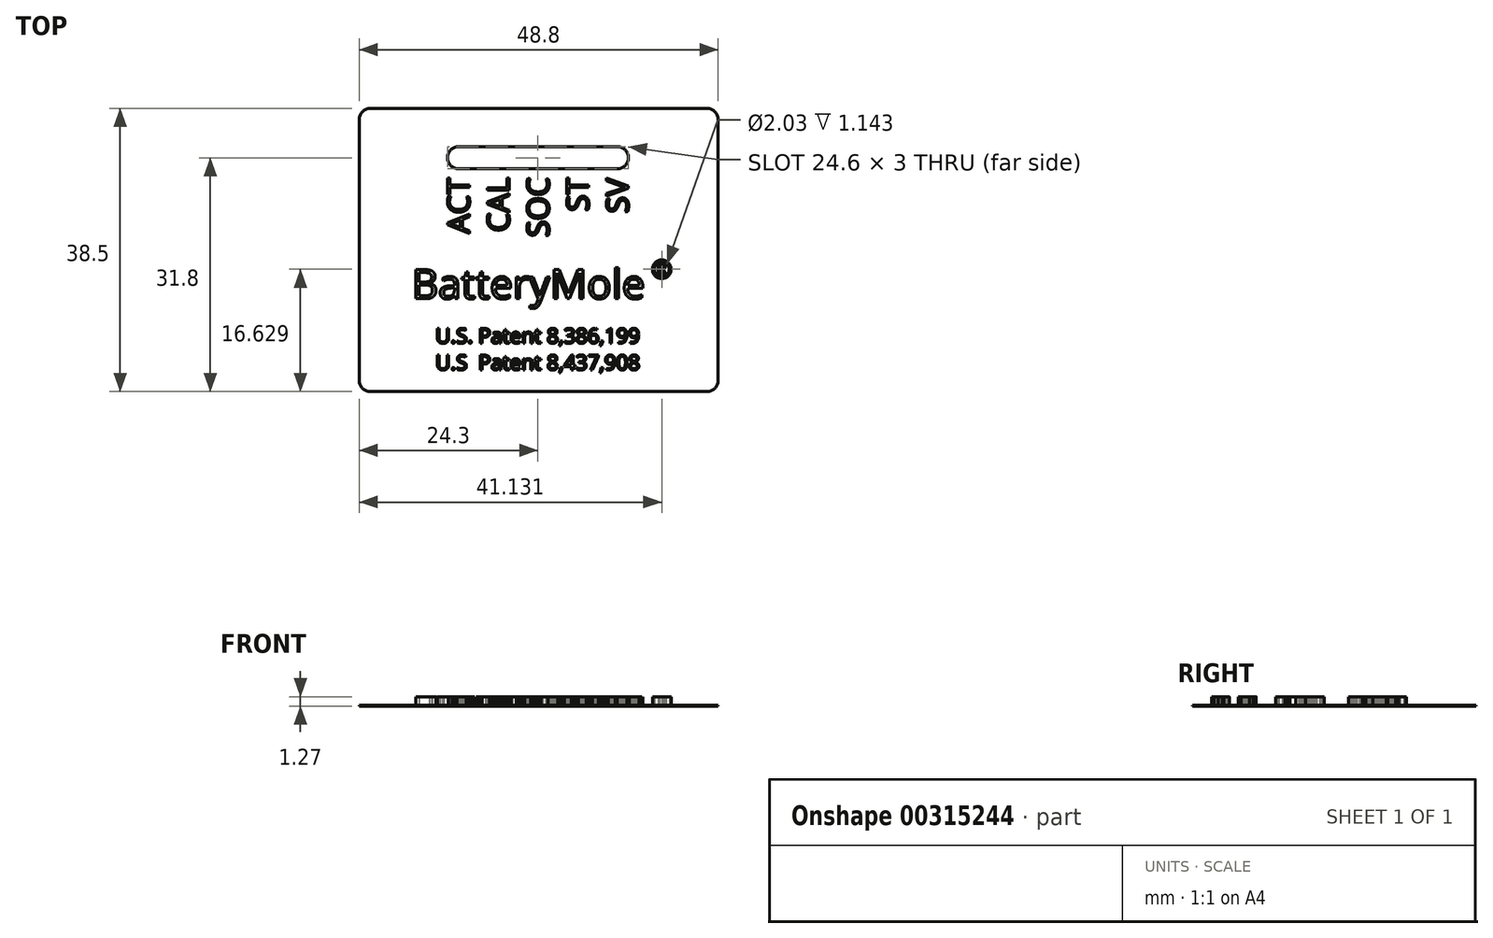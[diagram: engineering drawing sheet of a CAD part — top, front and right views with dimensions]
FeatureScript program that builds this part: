
annotation { "Feature Type Name" : "Feature", "Feature Type Description" : "" }
export const myFeature = defineFeature(function(context is Context, id is Id, definition is map)
    precondition{}
    {
        {
            var Q0;
            Q0=qCreatedBy(makeId("Top.planeOp"),FACE);
            var sketch = newSketch(context, id + "F0", { "sketchPlane" : qUnion([Q0])});
            skLineSegment(sketch, "E0.bottom", {"start": v(1.5, 38.5) * mm, "end": v(47.3, 38.5) * mm});
            skLineSegment(sketch, "E0.top", {"start": v(1.5, 0) * mm, "end": v(47.3, 0) * mm});
            skLineSegment(sketch, "E0.left", {"start": v(0, 37) * mm, "end": v(0, 1.5) * mm});
            skLineSegment(sketch, "E0.right", {"start": v(48.8, 37) * mm, "end": v(48.8, 1.5) * mm});
            skPoint(sketch, "E1.visualSharp", {"position": v(0, 38.5) * mm});
            skArc(sketch, "E1.filletArc", {"start": v(1.5, 38.5) * mm, "mid": v(0.44, 38.06) * mm, "end": v(0, 37) * mm});
            skPoint(sketch, "E2.visualSharp", {"position": v(48.8, 38.5) * mm});
            skArc(sketch, "E2.filletArc", {"start": v(48.8, 37) * mm, "mid": v(48.36, 38.06) * mm, "end": v(47.3, 38.5) * mm});
            skPoint(sketch, "E3.visualSharp", {"position": v(48.8, 0) * mm});
            skArc(sketch, "E3.filletArc", {"start": v(47.3, 0) * mm, "mid": v(48.36, 0.44) * mm, "end": v(48.8, 1.5) * mm});
            skPoint(sketch, "E4.visualSharp", {"position": v(0, 0) * mm});
            skArc(sketch, "E4.filletArc", {"start": v(0, 1.5) * mm, "mid": v(0.44, 0.44) * mm, "end": v(1.5, 0) * mm});
            skLineSegment(sketch, "E5", {"start": v(-1.94, 31.8) * mm, "end": v(50.94, 31.8) * mm, "construction": true});
            skPoint(sketch, "E6", {"position": v(0, 19.25) * mm});
            skLineSegment(sketch, "E7", {"start": v(24.3, 31.8) * mm, "end": v(24.3, 57.95) * mm, "construction": true});
            skLineSegment(sketch, "E8", {"start": v(41.58, 29.3) * mm, "end": v(3.43, 29.3) * mm, "construction": true});
            skArc(sketch, "E9", {"start": v(13.5, 33.3) * mm, "mid": v(12, 31.8) * mm, "end": v(13.5, 30.3) * mm});
            skArc(sketch, "E10", {"start": v(35.1, 33.3) * mm, "mid": v(36.6, 31.8) * mm, "end": v(35.1, 30.3) * mm});
            skLineSegment(sketch, "E11", {"start": v(13.5, 33.3) * mm, "end": v(35.1, 33.3) * mm});
            skLineSegment(sketch, "E12", {"start": v(35.1, 30.3) * mm, "end": v(13.5, 30.3) * mm});
            skSolve(sketch);
        }
        {
            var Q0;
            Q0=qCreatedBy(makeId("Top.planeOp"),FACE);
            var sketch = newSketch(context, id + "F1", { "sketchPlane" : qUnion([Q0])});
            skLineSegment(sketch, "E13.bottom", {"start": v(1.5, 38.5) * mm, "end": v(47.3, 38.5) * mm});
            skLineSegment(sketch, "E13.top", {"start": v(1.5, 0) * mm, "end": v(47.3, 0) * mm});
            skLineSegment(sketch, "E13.left", {"start": v(0, 37) * mm, "end": v(0, 1.5) * mm});
            skLineSegment(sketch, "E13.right", {"start": v(48.8, 37) * mm, "end": v(48.8, 1.5) * mm});
            skPoint(sketch, "E14.visualSharp", {"position": v(0, 38.5) * mm});
            skArc(sketch, "E14.filletArc", {"start": v(1.5, 38.5) * mm, "mid": v(0.44, 38.06) * mm, "end": v(0, 37) * mm});
            skPoint(sketch, "E15.visualSharp", {"position": v(48.8, 38.5) * mm});
            skArc(sketch, "E15.filletArc", {"start": v(48.8, 37) * mm, "mid": v(48.36, 38.06) * mm, "end": v(47.3, 38.5) * mm});
            skPoint(sketch, "E16.visualSharp", {"position": v(48.8, 0) * mm});
            skArc(sketch, "E16.filletArc", {"start": v(47.3, 0) * mm, "mid": v(48.36, 0.44) * mm, "end": v(48.8, 1.5) * mm});
            skPoint(sketch, "E17.visualSharp", {"position": v(0, 0) * mm});
            skArc(sketch, "E17.filletArc", {"start": v(0, 1.5) * mm, "mid": v(0.44, 0.44) * mm, "end": v(1.5, 0) * mm});
            skText(sketch, "E18", { "text": "BatteryMole", "fontName": "OpenSans-Regular.ttf"});
            skCircle(sketch, "E19", {"center": v(41.13, 16.63) * mm, "radius": 1.02 * mm});
            skCircle(sketch, "E20", {"center": v(41.13, 16.63) * mm, "radius": 1.27 * mm});
            skText(sketch, "E21", { "text": "U.S. Patent 8,386,199", "fontName": "OpenSans-Regular.ttf"});
            skText(sketch, "E22", { "text": "U.S. Patent 8,437,908", "fontName": "OpenSans-Regular.ttf"});
            skPoint(sketch, "E23", {"position": v(0, 19.25) * mm});
            skLineSegment(sketch, "E24", {"start": v(24.3, 16.46) * mm, "end": v(24.3, 31.8) * mm, "construction": true});
            skText(sketch, "E25", { "text": "ACT", "fontName": "OpenSans-Regular.ttf"});
            skText(sketch, "E26", { "text": "CAL", "fontName": "OpenSans-Regular.ttf"});
            skText(sketch, "E27", { "text": "SV", "fontName": "OpenSans-Regular.ttf"});
            skText(sketch, "E28", { "text": "ST", "fontName": "OpenSans-Regular.ttf"});
            skLineSegment(sketch, "E29", {"start": v(41.58, 29.3) * mm, "end": v(3.43, 29.3) * mm, "construction": true});
            skText(sketch, "E30", { "text": "R", "fontName": "OpenSans-Regular.ttf"});
            skText(sketch, "E31", { "text": "SOC", "fontName": "OpenSans-Regular.ttf"});
            skPoint(sketch, "E32", {"position": v(24.3, 21) * mm});
            const initialGuessF1  = {"E18": [0.00715, 0.01263, 1, 0, 0.004], "E21": [0.01037, 0.00658, 1, 0, 0.00203], "E22": [0.01037, 0.00295, 1, 0, 0.00203], "E25": [0.015, 0.0215, 0, 1, 0.003], "E26": [0.0204, 0.0217, 0, 1, 0.003], "E27": [0.0366, 0.02426, 0, 1, 0.003], "E28": [0.0312, 0.02448, 0, 1, 0.003], "E30": [0.04045, 0.0159, 1, 0, 0.0015], "E31": [0.0258, 0.021, 0, 1, 0.003]};
            skSetInitialGuess(sketch, initialGuessF1);
            skSolve(sketch);
        }
        {
            var Q0;
            Q0=makeQuery(id+"F0.imprint","IMPRINT",FACE,{"disambiguationData":[TD([[makeQuery(id+"F0.imprint","IMPRINT",EDGE,{"derivedFrom":sQuery(id+"F0.wireOp",EDGE,"E0.bottom")}),-1.0]])]});
            extrude(context, id + "F2", {"entities" : qUnion([Q0]), "depth" : 0.13 * mm});
        }
        {
            var Q0;
            Q0=makeQuery(id+"F1.imprint","IMPRINT",FACE,{"disambiguationData":[TD([[makeQuery(id+"F1.imprint","IMPRINT",EDGE,{"derivedFrom":sQuery(id+"F1.wireOp",EDGE,"E21.sketch_text.stroke-0")}),-1.0]])]});
            var Q1;
            Q1=makeQuery(id+"F1.imprint","IMPRINT",FACE,{"disambiguationData":[TD([[makeQuery(id+"F1.imprint","IMPRINT",EDGE,{"derivedFrom":sQuery(id+"F1.wireOp",EDGE,"E21.sketch_text.stroke-14")}),-1.0]])]});
            var Q2;
            Q2=makeQuery(id+"F1.imprint","IMPRINT",FACE,{"disambiguationData":[TD([[makeQuery(id+"F1.imprint","IMPRINT",EDGE,{"derivedFrom":sQuery(id+"F1.wireOp",EDGE,"E21.sketch_text.stroke-22")}),-1.0]])]});
            var Q3;
            Q3=makeQuery(id+"F1.imprint","IMPRINT",FACE,{"disambiguationData":[TD([[makeQuery(id+"F1.imprint","IMPRINT",EDGE,{"derivedFrom":sQuery(id+"F1.wireOp",EDGE,"E21.sketch_text.stroke-47")}),-1.0]])]});
            var Q4;
            Q4=makeQuery(id+"F1.imprint","IMPRINT",FACE,{"disambiguationData":[TD([[makeQuery(id+"F1.imprint","IMPRINT",EDGE,{"derivedFrom":sQuery(id+"F1.wireOp",EDGE,"E21.sketch_text.stroke-55")}),-1.0]])]});
            var Q5;
            Q5=makeQuery(id+"F1.imprint","IMPRINT",FACE,{"disambiguationData":[TD([[makeQuery(id+"F1.imprint","IMPRINT",EDGE,{"derivedFrom":sQuery(id+"F1.wireOp",EDGE,"E21.sketch_text.stroke-70")}),-1.0]])]});
            var Q6;
            Q6=makeQuery(id+"F1.imprint","IMPRINT",FACE,{"disambiguationData":[TD([[makeQuery(id+"F1.imprint","IMPRINT",EDGE,{"derivedFrom":sQuery(id+"F1.wireOp",EDGE,"E21.sketch_text.stroke-97")}),-1.0]])]});
            var Q7;
            Q7=makeQuery(id+"F1.imprint","IMPRINT",FACE,{"disambiguationData":[TD([[makeQuery(id+"F1.imprint","IMPRINT",EDGE,{"derivedFrom":sQuery(id+"F1.wireOp",EDGE,"E21.sketch_text.stroke-116")}),-1.0]])]});
            var Q8;
            Q8=makeQuery(id+"F1.imprint","IMPRINT",FACE,{"disambiguationData":[TD([[makeQuery(id+"F1.imprint","IMPRINT",EDGE,{"derivedFrom":sQuery(id+"F1.wireOp",EDGE,"E21.sketch_text.stroke-135")}),-1.0]])]});
            var Q9;
            Q9=makeQuery(id+"F1.imprint","IMPRINT",FACE,{"disambiguationData":[TD([[makeQuery(id+"F1.imprint","IMPRINT",EDGE,{"derivedFrom":sQuery(id+"F1.wireOp",EDGE,"E22.sketch_text.stroke-152")}),-1.0]])]});
            var Q10;
            Q10=makeQuery(id+"F1.imprint","IMPRINT",FACE,{"disambiguationData":[TD([[makeQuery(id+"F1.imprint","IMPRINT",EDGE,{"derivedFrom":sQuery(id+"F1.wireOp",EDGE,"E22.sketch_text.stroke-135")}),-1.0]])]});
            var Q11;
            Q11=makeQuery(id+"F1.imprint","IMPRINT",FACE,{"disambiguationData":[TD([[makeQuery(id+"F1.imprint","IMPRINT",EDGE,{"derivedFrom":sQuery(id+"F1.wireOp",EDGE,"E22.sketch_text.stroke-116")}),-1.0]])]});
            var Q12;
            Q12=makeQuery(id+"F1.imprint","IMPRINT",FACE,{"disambiguationData":[TD([[makeQuery(id+"F1.imprint","IMPRINT",EDGE,{"derivedFrom":sQuery(id+"F1.wireOp",EDGE,"E22.sketch_text.stroke-97")}),-1.0]])]});
            var Q13;
            Q13=makeQuery(id+"F1.imprint","IMPRINT",FACE,{"disambiguationData":[TD([[makeQuery(id+"F1.imprint","IMPRINT",EDGE,{"derivedFrom":sQuery(id+"F1.wireOp",EDGE,"E22.sketch_text.stroke-70")}),-1.0]])]});
            var Q14;
            Q14=makeQuery(id+"F1.imprint","IMPRINT",FACE,{"disambiguationData":[TD([[makeQuery(id+"F1.imprint","IMPRINT",EDGE,{"derivedFrom":sQuery(id+"F1.wireOp",EDGE,"E22.sketch_text.stroke-55")}),-1.0]])]});
            var Q15;
            Q15=makeQuery(id+"F1.imprint","IMPRINT",FACE,{"disambiguationData":[TD([[makeQuery(id+"F1.imprint","IMPRINT",EDGE,{"derivedFrom":sQuery(id+"F1.wireOp",EDGE,"E22.sketch_text.stroke-0")}),-1.0]])]});
            var Q16;
            Q16=makeQuery(id+"F1.imprint","IMPRINT",FACE,{"disambiguationData":[TD([[makeQuery(id+"F1.imprint","IMPRINT",EDGE,{"derivedFrom":sQuery(id+"F1.wireOp",EDGE,"E22.sketch_text.stroke-14")}),-1.0]])]});
            var Q17;
            Q17=makeQuery(id+"F1.imprint","IMPRINT",FACE,{"disambiguationData":[TD([[makeQuery(id+"F1.imprint","IMPRINT",EDGE,{"derivedFrom":sQuery(id+"F1.wireOp",EDGE,"E22.sketch_text.stroke-22")}),-1.0]])]});
            var Q18;
            Q18=makeQuery(id+"F1.imprint","IMPRINT",FACE,{"disambiguationData":[TD([[makeQuery(id+"F1.imprint","IMPRINT",EDGE,{"derivedFrom":sQuery(id+"F1.wireOp",EDGE,"E22.sketch_text.stroke-310")}),-1.0]])]});
            var Q19;
            Q19=makeQuery(id+"F1.imprint","IMPRINT",FACE,{"disambiguationData":[TD([[makeQuery(id+"F1.imprint","IMPRINT",EDGE,{"derivedFrom":sQuery(id+"F1.wireOp",EDGE,"E22.sketch_text.stroke-294")}),-1.0]])]});
            var Q20;
            Q20=makeQuery(id+"F1.imprint","IMPRINT",FACE,{"disambiguationData":[TD([[makeQuery(id+"F1.imprint","IMPRINT",EDGE,{"derivedFrom":sQuery(id+"F1.wireOp",EDGE,"E22.sketch_text.stroke-268")}),-1.0]])]});
            var Q21;
            Q21=makeQuery(id+"F1.imprint","IMPRINT",FACE,{"disambiguationData":[TD([[makeQuery(id+"F1.imprint","IMPRINT",EDGE,{"derivedFrom":sQuery(id+"F1.wireOp",EDGE,"E22.sketch_text.stroke-261")}),-1.0]])]});
            var Q22;
            Q22=makeQuery(id+"F1.imprint","IMPRINT",FACE,{"disambiguationData":[TD([[makeQuery(id+"F1.imprint","IMPRINT",EDGE,{"derivedFrom":sQuery(id+"F1.wireOp",EDGE,"E22.sketch_text.stroke-254")}),-1.0]])]});
            var Q23;
            Q23=makeQuery(id+"F1.imprint","IMPRINT",FACE,{"disambiguationData":[TD([[makeQuery(id+"F1.imprint","IMPRINT",EDGE,{"derivedFrom":sQuery(id+"F1.wireOp",EDGE,"E22.sketch_text.stroke-226")}),-1.0]])]});
            var Q24;
            Q24=makeQuery(id+"F1.imprint","IMPRINT",FACE,{"disambiguationData":[TD([[makeQuery(id+"F1.imprint","IMPRINT",EDGE,{"derivedFrom":sQuery(id+"F1.wireOp",EDGE,"E22.sketch_text.stroke-209")}),-1.0]])]});
            var Q25;
            Q25=makeQuery(id+"F1.imprint","IMPRINT",FACE,{"disambiguationData":[TD([[makeQuery(id+"F1.imprint","IMPRINT",EDGE,{"derivedFrom":sQuery(id+"F1.wireOp",EDGE,"E21.sketch_text.stroke-209")}),-1.0]])]});
            var Q26;
            Q26=makeQuery(id+"F1.imprint","IMPRINT",FACE,{"disambiguationData":[TD([[makeQuery(id+"F1.imprint","IMPRINT",EDGE,{"derivedFrom":sQuery(id+"F1.wireOp",EDGE,"E21.sketch_text.stroke-237")}),-1.0]])]});
            var Q27;
            Q27=makeQuery(id+"F1.imprint","IMPRINT",FACE,{"disambiguationData":[TD([[makeQuery(id+"F1.imprint","IMPRINT",EDGE,{"derivedFrom":sQuery(id+"F1.wireOp",EDGE,"E21.sketch_text.stroke-268")}),-1.0]])]});
            var Q28;
            Q28=makeQuery(id+"F1.imprint","IMPRINT",FACE,{"disambiguationData":[TD([[makeQuery(id+"F1.imprint","IMPRINT",EDGE,{"derivedFrom":sQuery(id+"F1.wireOp",EDGE,"E21.sketch_text.stroke-300")}),-1.0]])]});
            var Q29;
            Q29=makeQuery(id+"F1.imprint","IMPRINT",FACE,{"disambiguationData":[TD([[makeQuery(id+"F1.imprint","IMPRINT",EDGE,{"derivedFrom":sQuery(id+"F1.wireOp",EDGE,"E21.sketch_text.stroke-309")}),-1.0]])]});
            var Q30;
            Q30=makeQuery(id+"F1.imprint","IMPRINT",FACE,{"disambiguationData":[TD([[makeQuery(id+"F1.imprint","IMPRINT",EDGE,{"derivedFrom":sQuery(id+"F1.wireOp",EDGE,"E21.sketch_text.stroke-335")}),-1.0]])]});
            var Q31;
            Q31=makeQuery(id+"F1.imprint","IMPRINT",FACE,{"disambiguationData":[TD([[makeQuery(id+"F1.imprint","IMPRINT",EDGE,{"derivedFrom":sQuery(id+"F1.wireOp",EDGE,"E21.sketch_text.stroke-293")}),-1.0]])]});
            var Q32;
            Q32=makeQuery(id+"F1.imprint","IMPRINT",FACE,{"disambiguationData":[TD([[makeQuery(id+"F1.imprint","IMPRINT",EDGE,{"derivedFrom":sQuery(id+"F1.wireOp",EDGE,"E21.sketch_text.stroke-202")}),-1.0]])]});
            var Q33;
            Q33=makeQuery(id+"F1.imprint","IMPRINT",FACE,{"disambiguationData":[TD([[makeQuery(id+"F1.imprint","IMPRINT",EDGE,{"derivedFrom":sQuery(id+"F1.wireOp",EDGE,"E21.sketch_text.stroke-171")}),-1.0]])]});
            var Q34;
            Q34=makeQuery(id+"F1.imprint","IMPRINT",FACE,{"disambiguationData":[TD([[makeQuery(id+"F1.imprint","IMPRINT",EDGE,{"derivedFrom":sQuery(id+"F1.wireOp",EDGE,"E21.sketch_text.stroke-152")}),-1.0]])]});
            var Q35;
            Q35=makeQuery(id+"F1.imprint","IMPRINT",FACE,{"disambiguationData":[TD([[makeQuery(id+"F1.imprint","IMPRINT",EDGE,{"derivedFrom":sQuery(id+"F1.wireOp",EDGE,"E22.sketch_text.stroke-202")}),-1.0]])]});
            var Q36;
            Q36=makeQuery(id+"F1.imprint","IMPRINT",FACE,{"disambiguationData":[TD([[makeQuery(id+"F1.imprint","IMPRINT",EDGE,{"derivedFrom":sQuery(id+"F1.wireOp",EDGE,"E22.sketch_text.stroke-171")}),-1.0]])]});
            var Q37;
            Q37=makeQuery(id+"F1.imprint","IMPRINT",FACE,{"disambiguationData":[TD([[makeQuery(id+"F1.imprint","IMPRINT",EDGE,{"derivedFrom":sQuery(id+"F1.wireOp",EDGE,"E18.sketch_text.stroke-0")}),-1.0]])]});
            var Q38;
            Q38=makeQuery(id+"F1.imprint","IMPRINT",FACE,{"disambiguationData":[TD([[makeQuery(id+"F1.imprint","IMPRINT",EDGE,{"derivedFrom":sQuery(id+"F1.wireOp",EDGE,"E18.sketch_text.stroke-25")}),-1.0]])]});
            var Q39;
            Q39=makeQuery(id+"F1.imprint","IMPRINT",FACE,{"disambiguationData":[TD([[makeQuery(id+"F1.imprint","IMPRINT",EDGE,{"derivedFrom":sQuery(id+"F1.wireOp",EDGE,"E18.sketch_text.stroke-52")}),-1.0]])]});
            var Q40;
            Q40=makeQuery(id+"F1.imprint","IMPRINT",FACE,{"disambiguationData":[TD([[makeQuery(id+"F1.imprint","IMPRINT",EDGE,{"derivedFrom":sQuery(id+"F1.wireOp",EDGE,"E18.sketch_text.stroke-71")}),-1.0]])]});
            var Q41;
            Q41=makeQuery(id+"F1.imprint","IMPRINT",FACE,{"disambiguationData":[TD([[makeQuery(id+"F1.imprint","IMPRINT",EDGE,{"derivedFrom":sQuery(id+"F1.wireOp",EDGE,"E18.sketch_text.stroke-90")}),-1.0]])]});
            var Q42;
            Q42=makeQuery(id+"F1.imprint","IMPRINT",FACE,{"disambiguationData":[TD([[makeQuery(id+"F1.imprint","IMPRINT",EDGE,{"derivedFrom":sQuery(id+"F1.wireOp",EDGE,"E18.sketch_text.stroke-109")}),-1.0]])]});
            var Q43;
            Q43=makeQuery(id+"F1.imprint","IMPRINT",FACE,{"disambiguationData":[TD([[makeQuery(id+"F1.imprint","IMPRINT",EDGE,{"derivedFrom":sQuery(id+"F1.wireOp",EDGE,"E18.sketch_text.stroke-122")}),-1.0]])]});
            var Q44;
            Q44=makeQuery(id+"F1.imprint","IMPRINT",FACE,{"disambiguationData":[TD([[makeQuery(id+"F1.imprint","IMPRINT",EDGE,{"derivedFrom":sQuery(id+"F1.wireOp",EDGE,"E18.sketch_text.stroke-138")}),-1.0]])]});
            var Q45;
            Q45=makeQuery(id+"F1.imprint","IMPRINT",FACE,{"disambiguationData":[TD([[makeQuery(id+"F1.imprint","IMPRINT",EDGE,{"derivedFrom":sQuery(id+"F1.wireOp",EDGE,"E18.sketch_text.stroke-156")}),-1.0]])]});
            var Q46;
            Q46=makeQuery(id+"F1.imprint","IMPRINT",FACE,{"disambiguationData":[TD([[makeQuery(id+"F1.imprint","IMPRINT",EDGE,{"derivedFrom":sQuery(id+"F1.wireOp",EDGE,"E18.sketch_text.stroke-173")}),-1.0]])]});
            var Q47;
            Q47=makeQuery(id+"F1.imprint","IMPRINT",FACE,{"disambiguationData":[TD([[makeQuery(id+"F1.imprint","IMPRINT",EDGE,{"derivedFrom":sQuery(id+"F1.wireOp",EDGE,"E18.sketch_text.stroke-177")}),-1.0]])]});
            var Q48;
            Q48=makeQuery(id+"F1.imprint","IMPRINT",FACE,{"disambiguationData":[TD([[makeQuery(id+"F1.imprint","IMPRINT",EDGE,{"derivedFrom":sQuery(id+"F1.wireOp",EDGE,"E30.sketch_text.stroke-0")}),-1.0]])]});
            var Q49;
            Q49=makeQuery(id+"F1.imprint","IMPRINT",FACE,{"disambiguationData":[TD([[makeQuery(id+"F1.imprint","IMPRINT",EDGE,{"derivedFrom":sQuery(id+"F1.wireOp",EDGE,"E19")}),-1.0]])]});
            var Q50;
            Q50=makeQuery(id+"F1.imprint","IMPRINT",FACE,{"disambiguationData":[TD([[makeQuery(id+"F1.imprint","IMPRINT",EDGE,{"derivedFrom":sQuery(id+"F1.wireOp",EDGE,"E25.sketch_text.stroke-0")}),-1.0]])]});
            var Q51;
            Q51=makeQuery(id+"F1.imprint","IMPRINT",FACE,{"disambiguationData":[TD([[makeQuery(id+"F1.imprint","IMPRINT",EDGE,{"derivedFrom":sQuery(id+"F1.wireOp",EDGE,"E26.sketch_text.stroke-0")}),-1.0]])]});
            var Q52;
            Q52=makeQuery(id+"F1.imprint","IMPRINT",FACE,{"disambiguationData":[TD([[makeQuery(id+"F1.imprint","IMPRINT",EDGE,{"derivedFrom":sQuery(id+"F1.wireOp",EDGE,"E31.sketch_text.stroke-0")}),-1.0]])]});
            var Q53;
            Q53=makeQuery(id+"F1.imprint","IMPRINT",FACE,{"disambiguationData":[TD([[makeQuery(id+"F1.imprint","IMPRINT",EDGE,{"derivedFrom":sQuery(id+"F1.wireOp",EDGE,"E31.sketch_text.stroke-25")}),-1.0]])]});
            var Q54;
            Q54=makeQuery(id+"F1.imprint","IMPRINT",FACE,{"disambiguationData":[TD([[makeQuery(id+"F1.imprint","IMPRINT",EDGE,{"derivedFrom":sQuery(id+"F1.wireOp",EDGE,"E26.sketch_text.stroke-15")}),-1.0]])]});
            var Q55;
            Q55=makeQuery(id+"F1.imprint","IMPRINT",FACE,{"disambiguationData":[TD([[makeQuery(id+"F1.imprint","IMPRINT",EDGE,{"derivedFrom":sQuery(id+"F1.wireOp",EDGE,"E25.sketch_text.stroke-13")}),-1.0]])]});
            var Q56;
            Q56=makeQuery(id+"F1.imprint","IMPRINT",FACE,{"disambiguationData":[TD([[makeQuery(id+"F1.imprint","IMPRINT",EDGE,{"derivedFrom":sQuery(id+"F1.wireOp",EDGE,"E28.sketch_text.stroke-0")}),-1.0]])]});
            var Q57;
            Q57=makeQuery(id+"F1.imprint","IMPRINT",FACE,{"disambiguationData":[TD([[makeQuery(id+"F1.imprint","IMPRINT",EDGE,{"derivedFrom":sQuery(id+"F1.wireOp",EDGE,"E28.sketch_text.stroke-25")}),-1.0]])]});
            var Q58;
            Q58=makeQuery(id+"F1.imprint","IMPRINT",FACE,{"disambiguationData":[TD([[makeQuery(id+"F1.imprint","IMPRINT",EDGE,{"derivedFrom":sQuery(id+"F1.wireOp",EDGE,"E27.sketch_text.stroke-0")}),-1.0]])]});
            var Q59;
            Q59=makeQuery(id+"F1.imprint","IMPRINT",FACE,{"disambiguationData":[TD([[makeQuery(id+"F1.imprint","IMPRINT",EDGE,{"derivedFrom":sQuery(id+"F1.wireOp",EDGE,"E27.sketch_text.stroke-25")}),-1.0]])]});
            var Q60;
            Q60=makeQuery(id+"F1.imprint","IMPRINT",FACE,{"disambiguationData":[TD([[makeQuery(id+"F1.imprint","IMPRINT",EDGE,{"derivedFrom":sQuery(id+"F1.wireOp",EDGE,"E31.sketch_text.stroke-41")}),-1.0]])]});
            var Q61;
            Q61=makeQuery(id+"F1.imprint","IMPRINT",FACE,{"disambiguationData":[TD([[makeQuery(id+"F1.imprint","IMPRINT",EDGE,{"derivedFrom":sQuery(id+"F1.wireOp",EDGE,"E26.sketch_text.stroke-28")}),-1.0]])]});
            var Q62;
            Q62=makeQuery(id+"F1.imprint","IMPRINT",FACE,{"disambiguationData":[TD([[makeQuery(id+"F1.imprint","IMPRINT",EDGE,{"derivedFrom":sQuery(id+"F1.wireOp",EDGE,"E25.sketch_text.stroke-28")}),-1.0]])]});
            extrude(context, id + "F3", {"entities" : qUnion([Q0, Q1, Q2, Q3, Q4, Q5, Q6, Q7, Q8, Q9, Q10, Q11, Q12, Q13, Q14, Q15, Q16, Q17, Q18, Q19, Q20, Q21, Q22, Q23, Q24, Q25, Q26, Q27, Q28, Q29, Q30, Q31, Q32, Q33, Q34, Q35, Q36, Q37, Q38, Q39, Q40, Q41, Q42, Q43, Q44, Q45, Q46, Q47, Q48, Q49, Q50, Q51, Q52, Q53, Q54, Q55, Q56, Q57, Q58, Q59, Q60, Q61, Q62]), "operationType" : NewBodyOperationType.ADD, "depth" : 1.27 * mm});
        }
    });
